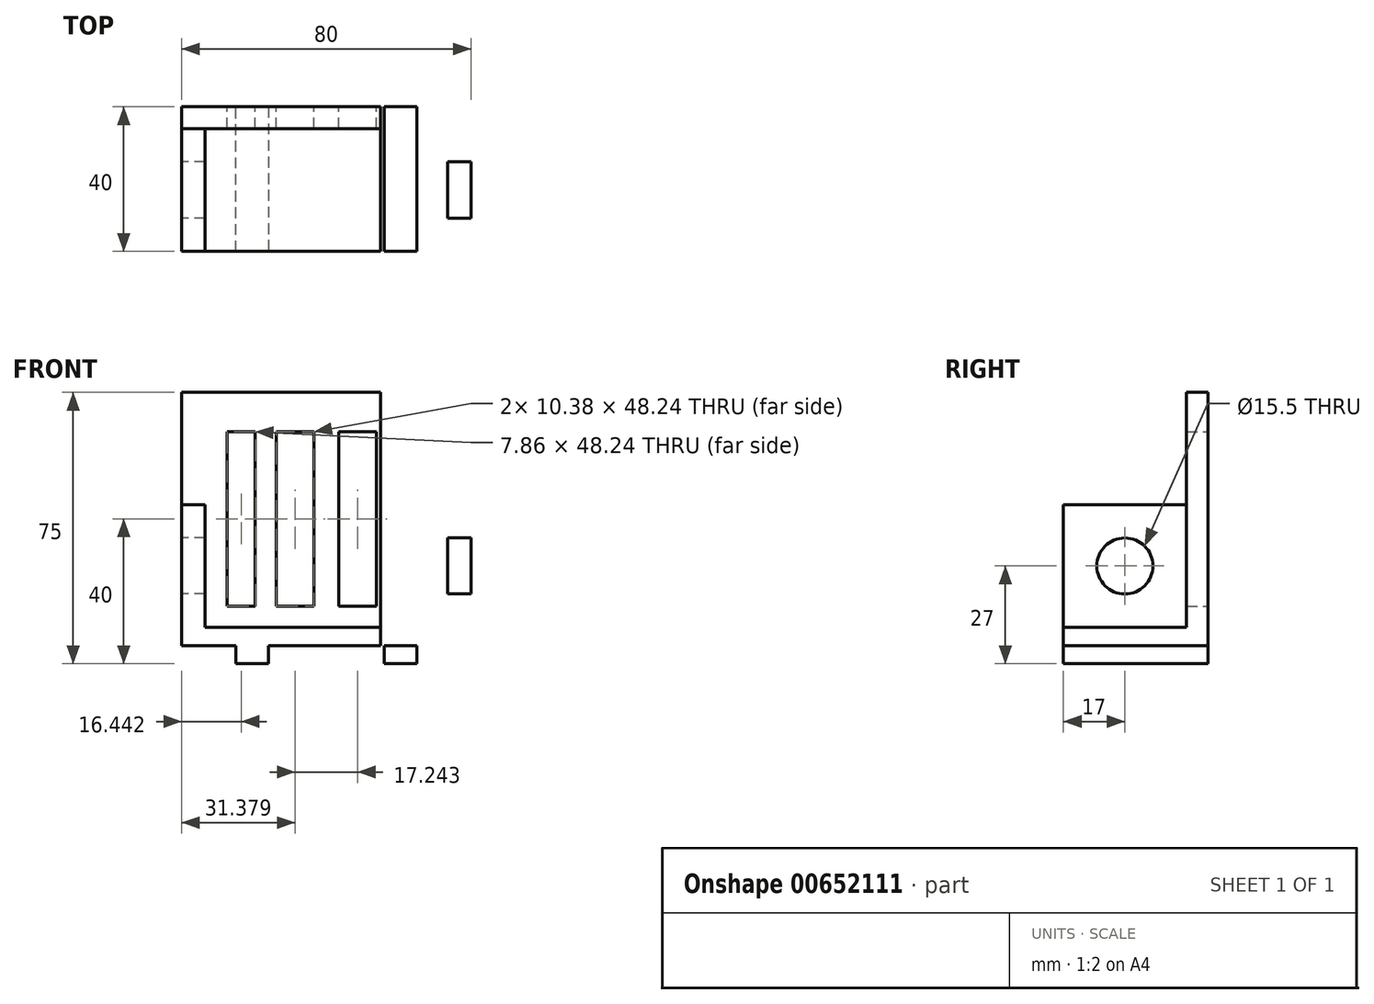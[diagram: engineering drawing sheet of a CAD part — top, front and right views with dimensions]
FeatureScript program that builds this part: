
annotation { "Feature Type Name" : "Feature", "Feature Type Description" : "" }
export const myFeature = defineFeature(function(context is Context, id is Id, definition is map)
    precondition{}
    {
        {
            var Q0;
            Q0=qCreatedBy(makeId("Top.planeOp"),FACE);
            var sketch = newSketch(context, id + "F0", { "sketchPlane" : qUnion([Q0])});
            skLineSegment(sketch, "E0.bottom", {"start": v(40, -30) * mm, "end": v(-40, -30) * mm});
            skLineSegment(sketch, "E0.top", {"start": v(40, 30) * mm, "end": v(-40, 30) * mm});
            skLineSegment(sketch, "E0.left", {"start": v(40, -30) * mm, "end": v(40, 30) * mm});
            skLineSegment(sketch, "E0.right", {"start": v(-40, -30) * mm, "end": v(-40, 30) * mm});
            skPoint(sketch, "E0.middle", {"position": v(0, 0) * mm});
            skSolve(sketch);
        }
        {
            var Q0;
            Q0=makeQuery(id+"F0.imprint","IMPRINT",FACE,{"disambiguationData":[TD([[makeQuery(id+"F0.imprint","IMPRINT",EDGE,{"derivedFrom":sQuery(id+"F0.wireOp",EDGE,"E0.bottom")}),-1.0]])]});
            extrude(context, id + "F1", {"entities" : qUnion([Q0]), "depth" : 10 * mm, "offsetDistance" : 25 * mm});
        }
        {
            var Q0;
            Q0=makeQuery(id+"F1.opExtrude","CAP_FACE",FACE,{"disambiguationData":[OSD([sQuery(id+"F0.wireOp",EDGE,"E0.bottom"),sQuery(id+"F0.wireOp",EDGE,"E0.top"),sQuery(id+"F0.wireOp",EDGE,"E0.left"),sQuery(id+"F0.wireOp",EDGE,"E0.right")])],"isStart":true});
            var sketch = newSketch(context, id + "F2", { "sketchPlane" : qUnion([Q0])});
            skLineSegment(sketch, "E1", {"start": v(-25, 30) * mm, "end": v(-25, -30) * mm});
            skLineSegment(sketch, "E2", {"start": v(25, 30) * mm, "end": v(25, -30) * mm});
            skLineSegment(sketch, "E3.bottom", {"start": v(16, -30) * mm, "end": v(-16, -30) * mm});
            skLineSegment(sketch, "E3.top", {"start": v(16, 30) * mm, "end": v(-16, 30) * mm});
            skLineSegment(sketch, "E3.left", {"start": v(16, -30) * mm, "end": v(16, 30) * mm});
            skLineSegment(sketch, "E3.right", {"start": v(-16, -30) * mm, "end": v(-16, 30) * mm});
            skPoint(sketch, "E3.middle", {"position": v(0, 0) * mm});
            skSolve(sketch);
        }
        {
            var Q0;
            {var subQ0=sQuery(id+"F2.wireOp",EDGE,"E2");Q0=makeQuery(id+"F2.imprint","IMPRINT",FACE,{"disambiguationData":[TD([[makeQuery(id+"F2.imprint","IMPRINT",EDGE,{"derivedFrom":subQ0}),1.0]])]});}
            var Q1;
            Q1=makeQuery(id+"F2.imprint","IMPRINT",FACE,{"disambiguationData":[TD([[makeQuery(id+"F2.imprint","IMPRINT",EDGE,{"derivedFrom":sQuery(id+"F2.wireOp",EDGE,"E3.bottom")}),-1.0]])]});
            var Q2;
            {var subQ0=sQuery(id+"F2.wireOp",EDGE,"E1");Q2=makeQuery(id+"F2.imprint","IMPRINT",FACE,{"disambiguationData":[TD([[makeQuery(id+"F2.imprint","IMPRINT",EDGE,{"derivedFrom":subQ0}),-1.0]])]});}
            extrude(context, id + "F3", {"entities" : qUnion([Q0, Q1, Q2]), "operationType" : NewBodyOperationType.REMOVE, "oppositeDirection" : true, "depth" : 5 * mm, "offsetDistance" : 25 * mm});
        }
        {
            var Q0;
            Q0=makeQuery(id+"F1.opExtrude","CAP_FACE",FACE,{"disambiguationData":[OSD([sQuery(id+"F0.wireOp",EDGE,"E0.bottom"),sQuery(id+"F0.wireOp",EDGE,"E0.top"),sQuery(id+"F0.wireOp",EDGE,"E0.left"),sQuery(id+"F0.wireOp",EDGE,"E0.right")])],"isStart":false});
            var sketch = newSketch(context, id + "F4", { "sketchPlane" : qUnion([Q0])});
            skLineSegment(sketch, "E4.bottom", {"start": v(40, 30) * mm, "end": v(-40, 30) * mm});
            skLineSegment(sketch, "E4.top", {"start": v(40, 24) * mm, "end": v(-40, 24) * mm});
            skLineSegment(sketch, "E4.left", {"start": v(40, 30) * mm, "end": v(40, 24) * mm});
            skLineSegment(sketch, "E4.right", {"start": v(-40, 30) * mm, "end": v(-40, 24) * mm});
            skLineSegment(sketch, "E5.bottom", {"start": v(40, -30) * mm, "end": v(-40, -30) * mm});
            skLineSegment(sketch, "E5.top", {"start": v(40, -24) * mm, "end": v(-40, -24) * mm});
            skLineSegment(sketch, "E5.left", {"start": v(40, -30) * mm, "end": v(40, -24) * mm});
            skLineSegment(sketch, "E5.right", {"start": v(-40, -30) * mm, "end": v(-40, -24) * mm});
            skSolve(sketch);
        }
        {
            var Q0;
            Q0=makeQuery(id+"F4.imprint","IMPRINT",FACE,{"disambiguationData":[TD([[makeQuery(id+"F4.imprint","IMPRINT",EDGE,{"derivedFrom":sQuery(id+"F4.wireOp",EDGE,"E4.bottom")}),1.0]])]});
            extrude(context, id + "F5", {"entities" : qUnion([Q0]), "operationType" : NewBodyOperationType.ADD, "depth" : 65 * mm, "offsetDistance" : 25 * mm});
        }
        {
            var Q0;
            Q0=makeQuery(id+"F5.boolean.opBoolean","MERGE",FACE,{"derivedFrom":[makeQuery(id+"F1.opExtrude","SWEPT_FACE",FACE,{"disambiguationData":[OSD([sQuery(id+"F0.wireOp",EDGE,"E0.bottom")])]}),makeQuery(id+"F5.opExtrude","SWEPT_FACE",FACE,{"disambiguationData":[OSD([sQuery(id+"F4.wireOp",EDGE,"E5.bottom")])]})]});
            var sketch = newSketch(context, id + "F6", { "sketchPlane" : qUnion([Q0])});
            skLineSegment(sketch, "E6", {"start": v(-40, 40) * mm, "end": v(40, 40) * mm, "construction": true});
            skLineSegment(sketch, "E7.bottom", {"start": v(27.5, 15.88) * mm, "end": v(-27.5, 15.88) * mm});
            skLineSegment(sketch, "E7.top", {"start": v(27.5, 64.12) * mm, "end": v(-27.5, 64.12) * mm});
            skLineSegment(sketch, "E7.left", {"start": v(27.5, 15.88) * mm, "end": v(27.5, 64.12) * mm});
            skLineSegment(sketch, "E7.right", {"start": v(-27.5, 15.88) * mm, "end": v(-27.5, 64.12) * mm});
            skPoint(sketch, "E7.middle", {"position": v(0, 40) * mm});
            skLineSegment(sketch, "E8.bottom", {"start": v(-19.63, 64.12) * mm, "end": v(-13.81, 64.12) * mm});
            skLineSegment(sketch, "E8.top", {"start": v(-19.63, 15.88) * mm, "end": v(-13.81, 15.88) * mm});
            skLineSegment(sketch, "E8.left", {"start": v(-19.63, 64.12) * mm, "end": v(-19.63, 15.88) * mm});
            skLineSegment(sketch, "E8.right", {"start": v(-13.81, 64.12) * mm, "end": v(-13.81, 15.88) * mm});
            skLineSegment(sketch, "E9.MirrorCS", {"start": v(13.81, 64.12) * mm, "end": v(13.81, 15.88) * mm});
            skLineSegment(sketch, "E10.MirrorCS", {"start": v(19.63, 64.12) * mm, "end": v(19.63, 15.88) * mm});
            skLineSegment(sketch, "E11.MirrorCS", {"start": v(19.63, 64.12) * mm, "end": v(13.81, 64.12) * mm});
            skLineSegment(sketch, "E12.MirrorCS", {"start": v(19.63, 15.88) * mm, "end": v(13.81, 15.88) * mm});
            skLineSegment(sketch, "E13.bottom", {"start": v(3.43, 15.88) * mm, "end": v(-3.43, 15.88) * mm});
            skLineSegment(sketch, "E13.top", {"start": v(3.43, 64.12) * mm, "end": v(-3.43, 64.12) * mm});
            skLineSegment(sketch, "E13.left", {"start": v(3.43, 15.88) * mm, "end": v(3.43, 64.12) * mm});
            skLineSegment(sketch, "E13.right", {"start": v(-3.43, 15.88) * mm, "end": v(-3.43, 64.12) * mm});
            skSolve(sketch);
        }
        {
            var Q0;
            Q0=makeQuery(id+"F5.boolean.opBoolean","MERGE",FACE,{"derivedFrom":[makeQuery(id+"F1.opExtrude","SWEPT_FACE",FACE,{"disambiguationData":[OSD([sQuery(id+"F0.wireOp",EDGE,"E0.top")])]}),makeQuery(id+"F5.opExtrude","SWEPT_FACE",FACE,{"disambiguationData":[OSD([sQuery(id+"F4.wireOp",EDGE,"E4.bottom")])]})]});
            var sketch = newSketch(context, id + "F7", { "sketchPlane" : qUnion([Q0])});
            skLineSegment(sketch, "E14.0", {"start": v(-27.5, 15.88) * mm, "end": v(-27.5, 64.12) * mm});
            skLineSegment(sketch, "E15.0", {"start": v(-19.63, 64.12) * mm, "end": v(-19.63, 15.88) * mm});
            skLineSegment(sketch, "E16.0", {"start": v(-27.5, 64.12) * mm, "end": v(27.5, 64.12) * mm});
            skLineSegment(sketch, "E17.0", {"start": v(-13.81, 64.12) * mm, "end": v(-13.81, 15.88) * mm});
            skLineSegment(sketch, "E18.0", {"start": v(-3.43, 15.88) * mm, "end": v(-3.43, 64.12) * mm});
            skLineSegment(sketch, "E19.0", {"start": v(-27.5, 15.88) * mm, "end": v(27.5, 15.88) * mm});
            skLineSegment(sketch, "E20.0", {"start": v(3.43, 15.88) * mm, "end": v(3.43, 64.12) * mm});
            skLineSegment(sketch, "E21.0", {"start": v(13.81, 64.12) * mm, "end": v(13.81, 15.88) * mm});
            skLineSegment(sketch, "E22.0", {"start": v(19.63, 64.12) * mm, "end": v(19.63, 15.88) * mm});
            skLineSegment(sketch, "E23.0", {"start": v(27.5, 15.88) * mm, "end": v(27.5, 64.12) * mm});
            skSolve(sketch);
        }
        {
            var Q0;
            {var subQ0=sQuery(id+"F7.wireOp",EDGE,"E14.0");Q0=makeQuery(id+"F7.imprint","IMPRINT",FACE,{"disambiguationData":[TD([[makeQuery(id+"F7.imprint","IMPRINT",EDGE,{"derivedFrom":subQ0}),-1.0]])]});}
            var Q1;
            {var subQ0=sQuery(id+"F7.wireOp",EDGE,"E17.0");Q1=makeQuery(id+"F7.imprint","IMPRINT",FACE,{"disambiguationData":[TD([[makeQuery(id+"F7.imprint","IMPRINT",EDGE,{"derivedFrom":subQ0}),1.0]])]});}
            var Q2;
            {var subQ0=sQuery(id+"F7.wireOp",EDGE,"E20.0");Q2=makeQuery(id+"F7.imprint","IMPRINT",FACE,{"disambiguationData":[TD([[makeQuery(id+"F7.imprint","IMPRINT",EDGE,{"derivedFrom":subQ0}),-1.0]])]});}
            var Q3;
            {var subQ2=sQuery(id+"F7.wireOp",EDGE,"E22.0");Q3=makeQuery(id+"F7.imprint","IMPRINT",FACE,{"disambiguationData":[TD([[makeQuery(id+"F7.imprint","IMPRINT",EDGE,{"derivedFrom":subQ2}),1.0]])]});}
            extrude(context, id + "F8", {"entities" : qUnion([Q0, Q1, Q2, Q3]), "operationType" : NewBodyOperationType.REMOVE, "oppositeDirection" : true, "depth" : 25 * mm, "offsetDistance" : 25 * mm});
        }
        {
            var Q0;
            Q0=makeQuery(id+"F1.opExtrude","CAP_FACE",FACE,{"disambiguationData":[OSD([sQuery(id+"F0.wireOp",EDGE,"E0.bottom"),sQuery(id+"F0.wireOp",EDGE,"E0.top"),sQuery(id+"F0.wireOp",EDGE,"E0.left"),sQuery(id+"F0.wireOp",EDGE,"E0.right")])],"isStart":false});
            var sketch = newSketch(context, id + "F9", { "sketchPlane" : qUnion([Q0])});
            skLineSegment(sketch, "E24.bottom", {"start": v(-40, 24) * mm, "end": v(-33.48, 24) * mm});
            skLineSegment(sketch, "E24.top", {"start": v(-40, -10) * mm, "end": v(-33.48, -10) * mm});
            skLineSegment(sketch, "E24.left", {"start": v(-40, 24) * mm, "end": v(-40, -10) * mm});
            skLineSegment(sketch, "E24.right", {"start": v(-33.48, 24) * mm, "end": v(-33.48, -10) * mm});
            skLineSegment(sketch, "E25.MirrorCS", {"start": v(33.48, 24) * mm, "end": v(33.48, -10) * mm});
            skLineSegment(sketch, "E26.MirrorCS", {"start": v(40, 24) * mm, "end": v(33.48, 24) * mm});
            skLineSegment(sketch, "E27.MirrorCS", {"start": v(40, 24) * mm, "end": v(40, -10) * mm});
            skLineSegment(sketch, "E28.MirrorCS", {"start": v(40, -10) * mm, "end": v(33.48, -10) * mm});
            skSolve(sketch);
        }
        {
            var Q0;
            Q0=makeQuery(id+"F9.imprint","IMPRINT",FACE,{"disambiguationData":[TD([[makeQuery(id+"F9.imprint","IMPRINT",EDGE,{"derivedFrom":sQuery(id+"F9.wireOp",EDGE,"E24.bottom")}),1.0]])]});
            var Q1;
            Q1=makeQuery(id+"F9.imprint","IMPRINT",FACE,{"disambiguationData":[TD([[makeQuery(id+"F9.imprint","IMPRINT",EDGE,{"derivedFrom":sQuery(id+"F9.wireOp",EDGE,"E25.MirrorCS")}),1.0]])]});
            extrude(context, id + "F10", {"entities" : qUnion([Q0, Q1]), "operationType" : NewBodyOperationType.ADD, "depth" : 34 * mm, "offsetDistance" : 25 * mm});
        }
        {
            var Q0;
            Q0=makeQuery(id+"F10.boolean.opBoolean","MERGE",FACE,{"derivedFrom":[makeQuery(id+"F5.boolean.opBoolean","MERGE",FACE,{"derivedFrom":[makeQuery(id+"F1.opExtrude","SWEPT_FACE",FACE,{"disambiguationData":[OSD([sQuery(id+"F0.wireOp",EDGE,"E0.right")])]}),makeQuery(id+"F5.opExtrude","SWEPT_FACE",FACE,{"disambiguationData":[OSD([sQuery(id+"F4.wireOp",EDGE,"E4.right")])]})]}),makeQuery(id+"F10.opExtrude","SWEPT_FACE",FACE,{"disambiguationData":[OSD([sQuery(id+"F9.wireOp",EDGE,"E24.left")])]})]});
            var sketch = newSketch(context, id + "F11", { "sketchPlane" : qUnion([Q0])});
            skLineSegment(sketch, "E29", {"start": v(10, 10) * mm, "end": v(-30, 10) * mm, "construction": true});
            skLineSegment(sketch, "E30", {"start": v(-24, 44) * mm, "end": v(-24, 10) * mm, "construction": true});
            skLineSegment(sketch, "E31", {"start": v(-24, 10) * mm, "end": v(10, 44) * mm, "construction": true});
            skLineSegment(sketch, "E32", {"start": v(-24, 44) * mm, "end": v(10, 10) * mm, "construction": true});
            skCircle(sketch, "E33", {"center": v(-7, 27) * mm, "radius": 7.75 * mm});
            skSolve(sketch);
        }
        {
            var Q0;
            Q0=makeQuery(id+"F10.boolean.opBoolean","MERGE",FACE,{"derivedFrom":[makeQuery(id+"F5.boolean.opBoolean","MERGE",FACE,{"derivedFrom":[makeQuery(id+"F1.opExtrude","SWEPT_FACE",FACE,{"disambiguationData":[OSD([sQuery(id+"F0.wireOp",EDGE,"E0.left")])]}),makeQuery(id+"F5.opExtrude","SWEPT_FACE",FACE,{"disambiguationData":[OSD([sQuery(id+"F4.wireOp",EDGE,"E4.left")])]})]}),makeQuery(id+"F10.opExtrude","SWEPT_FACE",FACE,{"disambiguationData":[OSD([sQuery(id+"F9.wireOp",EDGE,"E27.MirrorCS")])]})]});
            var sketch = newSketch(context, id + "F12", { "sketchPlane" : qUnion([Q0])});
            skLineSegment(sketch, "E34.0.0", {"start": v(-30, 10) * mm, "end": v(-30, 5) * mm});
            skLineSegment(sketch, "E34.0.1", {"start": v(-30, 5) * mm, "end": v(30, 5) * mm});
            skLineSegment(sketch, "E34.0.2", {"start": v(30, 5) * mm, "end": v(30, 75) * mm});
            skLineSegment(sketch, "E34.0.3", {"start": v(30, 75) * mm, "end": v(24, 75) * mm});
            skLineSegment(sketch, "E34.0.4", {"start": v(24, 75) * mm, "end": v(24, 44) * mm});
            skLineSegment(sketch, "E34.0.5", {"start": v(24, 44) * mm, "end": v(-10, 44) * mm});
            skLineSegment(sketch, "E34.0.6", {"start": v(-10, 44) * mm, "end": v(-10, 10) * mm});
            skLineSegment(sketch, "E34.0.7", {"start": v(-10, 10) * mm, "end": v(-30, 10) * mm});
            skCircle(sketch, "E35.0", {"center": v(7, 27) * mm, "radius": 7.75 * mm});
            skSolve(sketch);
        }
        {
            var Q0;
            Q0=makeQuery(id+"F11.imprint","IMPRINT",FACE,{"disambiguationData":[TD([[makeQuery(id+"F11.imprint","IMPRINT",EDGE,{"derivedFrom":sQuery(id+"F11.wireOp",EDGE,"E33")}),1.0]])]});
            extrude(context, id + "F13", {"entities" : qUnion([Q0]), "operationType" : NewBodyOperationType.REMOVE, "oppositeDirection" : true, "depth" : 25 * mm, "offsetDistance" : 25 * mm});
        }
        {
            var Q0;
            {var subQ1=sQuery(id+"F0.wireOp",EDGE,"E0.left");var subQ2=sQuery(id+"F0.wireOp",EDGE,"E0.bottom");var subQ3=sQuery(id+"F4.wireOp",EDGE,"E4.left");var subQ7=sQuery(id+"F9.wireOp",EDGE,"E27.MirrorCS");Q0=makeQuery(id+"FMMbyH0mWgR35c4_1.boolean.opBoolean","SPLIT",FACE,{"disambiguationData":[TD([makeQuery(id+"F1.opExtrude","SWEPT_FACE",FACE,{"disambiguationData":[OSD([subQ2])]})])],"derivedFrom":makeQuery(id+"F10.boolean.opBoolean","MERGE",FACE,{"derivedFrom":[makeQuery(id+"F5.boolean.opBoolean","MERGE",FACE,{"derivedFrom":[makeQuery(id+"F1.opExtrude","SWEPT_FACE",FACE,{"disambiguationData":[OSD([subQ1])]}),makeQuery(id+"F5.opExtrude","SWEPT_FACE",FACE,{"disambiguationData":[OSD([subQ3])]})]}),makeQuery(id+"F10.opExtrude","SWEPT_FACE",FACE,{"disambiguationData":[OSD([subQ7])]})]})});}
            var sketch = newSketch(context, id + "F14", { "sketchPlane" : qUnion([Q0])});
            skLineSegment(sketch, "E36", {"start": v(-10, 10) * mm, "end": v(-10, 0) * mm});
            skPoint(sketch, "E37", {"position": v(-10, 5) * mm});
            skSolve(sketch);
        }
        {
            var Q0;
            {var subQ1=sQuery(id+"F0.wireOp",EDGE,"E0.left");var subQ2=makeQuery(id+"F1.opExtrude","CAP_EDGE",EDGE,{"disambiguationData":[OSD([subQ1])],"isStart":false});Q0=makeQuery(id+"F14.imprint","IMPRINT",FACE,{"disambiguationData":[TD([[makeQuery(id+"F14.imprint","IMPRINT",EDGE,{"derivedFrom":subQ2}),-1.0]])]});}
            extrude(context, id + "F15", {"entities" : qUnion([Q0]), "operationType" : NewBodyOperationType.REMOVE, "oppositeDirection" : true, "depth" : 90 * mm, "offsetDistance" : 25 * mm});
        }
        {
            var Q0;
            Q0=makeQuery(id+"F3.boolean.opBoolean","COPY",FACE,{"derivedFrom":makeQuery(id+"F3.opExtrude","SWEPT_FACE",FACE,{"disambiguationData":[OSD([sQuery(id+"F2.wireOp",EDGE,"E2")])]})});
            var sketch = newSketch(context, id + "F16", { "sketchPlane" : qUnion([Q0])});
            skLineSegment(sketch, "E38", {"start": v(-10, 5) * mm, "end": v(-10, 0) * mm});
            skSolve(sketch);
        }
        {
            var Q0;
            {var subQ0=sQuery(id+"F16.wireOp",EDGE,"E38");Q0=makeQuery(id+"F16.imprint","IMPRINT",FACE,{"disambiguationData":[TD([[makeQuery(id+"F16.imprint","IMPRINT",EDGE,{"derivedFrom":subQ0}),-1.0]])]});}
            extrude(context, id + "F17", {"entities" : qUnion([Q0]), "operationType" : NewBodyOperationType.REMOVE, "oppositeDirection" : true, "depth" : 25 * mm, "offsetDistance" : 25 * mm});
        }
        {
            var Q0;
            Q0=makeQuery(id+"F3.boolean.opBoolean","COPY",FACE,{"derivedFrom":makeQuery(id+"F3.opExtrude","SWEPT_FACE",FACE,{"disambiguationData":[OSD([sQuery(id+"F2.wireOp",EDGE,"E1")])]})});
            var sketch = newSketch(context, id + "F18", { "sketchPlane" : qUnion([Q0])});
            skLineSegment(sketch, "E39", {"start": v(10, 5) * mm, "end": v(10, 0) * mm});
            skSolve(sketch);
        }
        {
            var Q0;
            {var subQ0=sQuery(id+"F18.wireOp",EDGE,"E39");Q0=makeQuery(id+"F18.imprint","IMPRINT",FACE,{"disambiguationData":[TD([[makeQuery(id+"F18.imprint","IMPRINT",EDGE,{"derivedFrom":subQ0}),1.0]])]});}
            extrude(context, id + "F19", {"entities" : qUnion([Q0]), "operationType" : NewBodyOperationType.REMOVE, "oppositeDirection" : true, "depth" : 25 * mm, "offsetDistance" : 25 * mm});
        }
        {
            var Q0;
            Q0=makeQuery(id+"F12.imprint","IMPRINT",FACE,{"disambiguationData":[TD([[makeQuery(id+"F12.imprint","IMPRINT",EDGE,{"derivedFrom":sQuery(id+"F12.wireOp",EDGE,"E35.0")}),-1.0]])]});
            extrude(context, id + "F20", {"entities" : qUnion([Q0]), "operationType" : NewBodyOperationType.REMOVE, "oppositeDirection" : true, "depth" : 25 * mm, "offsetDistance" : 25 * mm});
        }
    });
